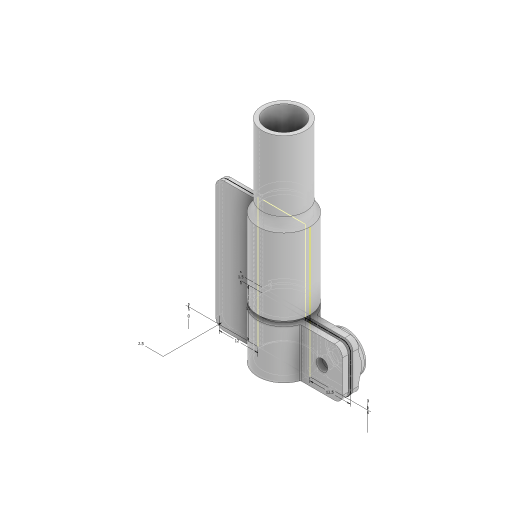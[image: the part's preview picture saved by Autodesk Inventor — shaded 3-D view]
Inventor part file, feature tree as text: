
AUTODESK INVENTOR PART (.ipt)
format: ipt  version: 2023 (Build 270158000, 158)  size: 265,216 bytes
history: native  units: mm
features: extrude x8, sketch x6, fillet x5, chamfer x1
ambient origin geometry x8: Origin, YZ Plane, XZ Plane, XY Plane, X Axis, Y Axis, Z Axis, Center Point
bodies: Solid1 (feature_tree)
feature tree (20):
  extrude  "Extrusion1"  Depth=16.0mm
  extrude  "Extrusion2"  Depth=40.0mm TaperAngle=0.0deg
  fillet  "Fillet1"  Radius=13.3mm
  fillet  "Fillet2"  Radius=10.8mm
  sketch  "Sketch3"  dims[d7=25.0mm d8=0.0mm d9=5.0mm]
  extrude  "Extrusion3"  Depth=5.0mm
  extrude  "Extrusion4"  Depth=12.0mm
  extrude  "Extrusion5"  Depth=15.0mm
  extrude  "Extrusion6"  TaperAngle=0.0deg  [1 undecoded]
  fillet  "Fillet3"  Radius=12.5mm
  fillet  "Fillet4"  Radius=2.5mm
  extrude  "Extrusion7"  Depth=0.5mm TaperAngle=0.0deg
  fillet  "Fillet5"  Radius=5.0mm
  extrude  "Extrusion8"  Depth=0.5mm
  chamfer  "Chamfer1"  Distance=0.75mm
  sketch  "Sketch1"  dims[d0=13.1mm d1=16.0mm]
  sketch  "Sketch2"  dims[d2=1.45mm d3=40.0mm d4=0.0mm d5=13.3mm d6=10.8mm]
  sketch  "Sketch4"  dims[d10=3.0mm d11=12.0mm]
  sketch  "Sketch5"  dims[d12=0.0mm d13=15.0mm]
  sketch  "Sketch6"  dims[d14=1.5mm d15=0.0mm d16=12.5mm d17=2.5mm d18=2.0mm d19=0.0mm d20=5.0mm d21=0.0mm d22=1.5mm d23=0.75mm d24=15.0mm d25=0.0mm d26=0.0mm d27=0.0mm d28=0.5mm d29=0.5mm d30=12.0mm d31=6.25mm d32=15.0mm d33=7.5mm d34=5.7mm d35=2.5mm d36=0.0mm d37=2.0mm d38=3.5mm d39=0.0mm d40=0.0mm d41=1.0mm d42=2.0mm d43=45.0deg]
note: 1 required parameter value undecoded (feature->parameter linkage not recoverable at this tier; creation-order binding heuristic only, values carry confidence <= 0.55)
